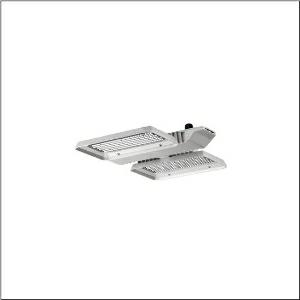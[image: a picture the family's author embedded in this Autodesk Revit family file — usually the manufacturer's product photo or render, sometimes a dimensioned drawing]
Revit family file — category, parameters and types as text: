
# Revit family: highbay_11_51hla2d14fca
name_source: partatom
category: Lighting Fixtures
units: mm (PartAtom-declared; Revit-internal decimal feet)

## family parameters
Cut with Voids When Loaded = No
Host = Face
Light Source = No
Part Type = Normal
Room Calculation Point = No
Round Connector Dimension = Use Diameter
Shared = No

## types (1)
- --- (1 x LED, 14400 lm, 81.2 W, 4000K)
    Apparent Load = 81 VA
    CIE Flux Codes = 89 96 99 100 100
    Color Rendering = 80
    Color Temperature = 4000K
    Default Elevation = 1800 mm
    Description = Highbay 11, LED high bay luminaire, primary light control with lens, of PMMA, light emission: direct distribution, primary light characteristic: symmetric, installation type: surface-mounted, suspended mounting, for 1x 2 x LED rated luminous flux: 14.400 lm, light colour: 840, colour temperature: 4000K, control gear: ECG DALI, with terminal, 5-pole, max. 2.5mm², mains connection: 230..240V, AC, 50/60Hz, rated input power: 81W, LED unit, of diecast aluminium, unplated, bead blasted, silver, length: 470 mm, width: 500 mm, height: 65mm, housing, of diecast aluminium, uncoated, bead blasted, silver, protection rating (complete): IP65, insulation class (complete): insulation class I (protective earthing), certification: CE, ENEC, VDE, protection symbol: D, impact resistance: IK08 with glass or PC cover, permissible ambient temperature for indoor applications: -35..+55°C, reducing of maximum allowable ambient temperature of 5°C with ceiling mounting, corresponds to IFS (International Featured Standards) requirements for safety and quality in the food industry, packaging unit: 1 piece
    Height = 95 mm
    Lamp = 1 x LED
    Lamp Light Flux = 14400 lm
    Lamp Power = 81.2 W
    Lamp count = 1
    Length = 468 mm
    Luminous efficacy = 177 lm/W
    Manufacturer = Siteco
    ModVariant = No
    Model = 51HLA2D14FCA
    Mounting Place = Ceiling
    Mounting Type = Pendant
    Number of Poles = 1
    OnlyDefault = Yes
    Power Factor = 1
    Product Name = Highbay 11
    Product group = LED high bay luminaire
    ProductGroupID = 903
    Protection Class = Protection class I
    Protection Degree = IP 65
    RLX_Detail_Level = 1
    RlxData = <blob elided: 85689 chars, md5=8d83f399>
    Socket = socket
    Standby Power = 0 W
    System Light Flux = 14400 lm
    System Power = 81 W
    Type Comments = factory setting: luminous flux: 100 % | dim-lin: 254 | 460 mA
    Type Image = l_1003425.jpg
    URL = http://relux.com
    VarID = @adj_140935
    Voltage = 0 V
    Weight = 0.00 kg
    Width = 501 mm

## geometry (parser evidence)
native form markers: Blend x4, Sweep x12
no freeform markers — native parametric forms only
